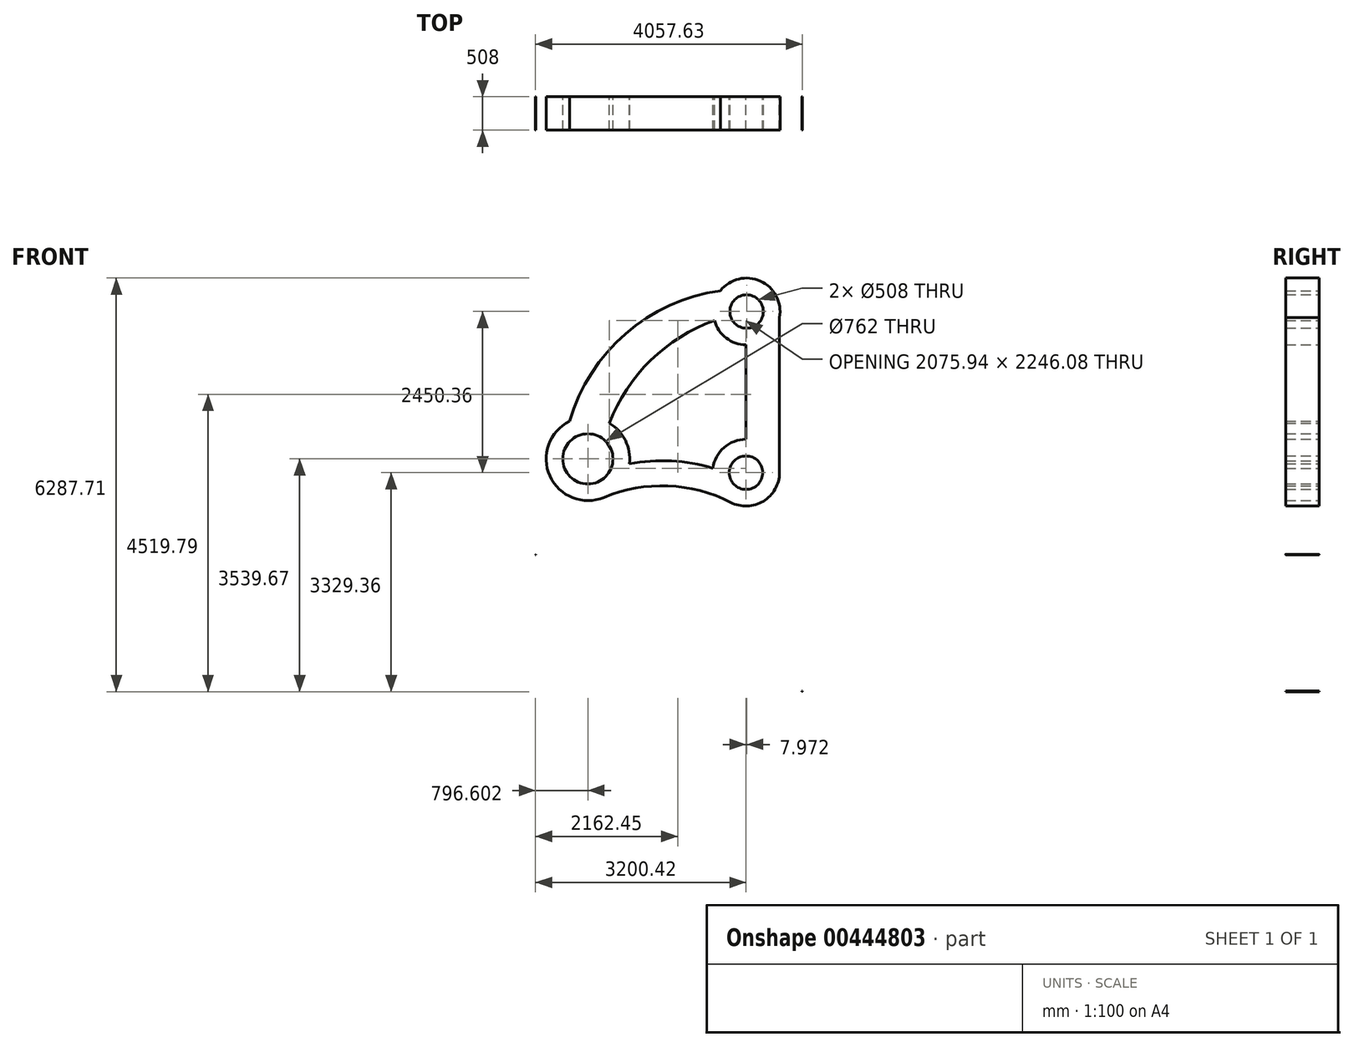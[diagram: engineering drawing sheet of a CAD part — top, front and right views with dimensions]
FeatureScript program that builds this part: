
annotation { "Feature Type Name" : "Feature", "Feature Type Description" : "" }
export const myFeature = defineFeature(function(context is Context, id is Id, definition is map)
    precondition{}
    {
        {
            var Q0;
            Q0=qCreatedBy(makeId("Front.planeOp"),FACE);
            var sketch = newSketch(context, id + "F0", { "sketchPlane" : qUnion([Q0])});
            skCircle(sketch, "E0", {"center": v(0, 0) * mm, "radius": 254 * mm});
            skArc(sketch, "E1", {"start": v(-294.4, -414) * mm, "mid": v(267.89, -431.62) * mm, "end": v(501.65, 80.07) * mm});
            skLineSegment(sketch, "E2", {"start": v(0, 0) * mm, "end": v(0, 508) * mm});
            skCircle(sketch, "E3", {"center": v(7.97, 2450.35) * mm, "radius": 254 * mm});
            skArc(sketch, "E4", {"start": v(-481.24, 2313.47) * mm, "mid": v(505.87, 2349.57) * mm, "end": v(-389.5, 2766.72) * mm});
            skLineSegment(sketch, "E5", {"start": v(508, 2540) * mm, "end": v(508, 0) * mm});
            skArc(sketch, "E6", {"start": v(-2779.82, -281.18) * mm, "mid": v(-2778.69, -292.14) * mm, "end": v(-2777.51, -303.1) * mm});
            skCircle(sketch, "E7", {"center": v(-2403.82, 210.3) * mm, "radius": 381 * mm});
            skArc(sketch, "E8", {"start": v(-1773.21, 135.7) * mm, "mid": v(-2933.68, 560.27) * mm, "end": v(-2087.68, -340.4) * mm});
            skLineSegment(sketch, "E9.0", {"start": v(501.65, 2540) * mm, "end": v(501.65, 0) * mm});
            skArc(sketch, "E10.0", {"start": v(-3196.17, -1241.99) * mm, "mid": v(-3196.17, -1242) * mm, "end": v(-3196.17, -1242) * mm});
            skArc(sketch, "E11.0", {"start": v(-3200.42, -1248.58) * mm, "mid": v(-3200.42, -1248.58) * mm, "end": v(-3200.42, -1248.58) * mm});
            skArc(sketch, "E12", {"start": v(-3196.17, -1242) * mm, "mid": v(-3198.3, -1245.28) * mm, "end": v(-3200.42, -1248.58) * mm});
            skArc(sketch, "E13.trimOffspring", {"start": v(0, 508) * mm, "mid": v(-343.2, 374.54) * mm, "end": v(-506.07, 44.28) * mm});
            skLineSegment(sketch, "E14.trimOffspring", {"start": v(-1699.09, 148.65) * mm, "end": v(-1771.23, 154.96) * mm});
            skLineSegment(sketch, "E15", {"start": v(0, 508) * mm, "end": v(0, 1942.42) * mm});
            skArc(sketch, "E16.trimOffspring", {"start": v(-3336.76, -789.98) * mm, "mid": v(-3339.3, -793.07) * mm, "end": v(-3341.82, -796.15) * mm});
            skArc(sketch, "E17.trimOffspring", {"start": v(-3196.17, -1241.99) * mm, "mid": v(-3198.3, -1245.28) * mm, "end": v(-3200.42, -1248.58) * mm});
            skArc(sketch, "E18.trimOffspring", {"start": v(846.77, -3329.36) * mm, "mid": v(848.22, -3325.71) * mm, "end": v(849.65, -3322.07) * mm});
            skArc(sketch, "E19.trimOffspring", {"start": v(846.74, -3329.36) * mm, "mid": v(848.19, -3325.72) * mm, "end": v(849.63, -3322.07) * mm});
            skArc(sketch, "E20.trimOffspring", {"start": v(854.34, -3327.42) * mm, "mid": v(855.78, -3323.77) * mm, "end": v(857.21, -3320.12) * mm});
            skArc(sketch, "E21.trimOffspring", {"start": v(-232.28, -451.79) * mm, "mid": v(-1187.2, -200.6) * mm, "end": v(-2158.97, -375.6) * mm});
            skArc(sketch, "E22.trimOffspring", {"start": v(-230.3, -452.8) * mm, "mid": v(-1186.09, -200.65) * mm, "end": v(-2158.97, -375.6) * mm});
            skArc(sketch, "E23.trimOffspring", {"start": v(-294.4, -414) * mm, "mid": v(-1262.87, -192.52) * mm, "end": v(-2234.1, -401.6) * mm});
            skArc(sketch, "E24", {"start": v(-481.24, 2313.47) * mm, "mid": v(-1449.42, 1708.5) * mm, "end": v(-2075.94, 754.1) * mm});
            skArc(sketch, "E25.trimOffspring", {"start": v(1296.97, -3181.12) * mm, "mid": v(1298, -3177.26) * mm, "end": v(1299.04, -3173.41) * mm});
            skArc(sketch, "E26.trimOffspring", {"start": v(-503.51, 67.39) * mm, "mid": v(-1134.23, 178.32) * mm, "end": v(-1773.21, 135.7) * mm});
            skArc(sketch, "E27.trimOffspring", {"start": v(-389.5, 2766.72) * mm, "mid": v(-1829.08, 2112.08) * mm, "end": v(-2682.68, 780.8) * mm});
            skArc(sketch, "E28.trimOffspring", {"start": v(846.74, -3329.36) * mm, "mid": v(850.54, -3328.4) * mm, "end": v(854.34, -3327.42) * mm});
            skArc(sketch, "E29.trimOffspring", {"start": v(849.63, -3322.07) * mm, "mid": v(853.42, -3321.1) * mm, "end": v(857.21, -3320.12) * mm});
            skSolve(sketch);
        }
        {
            var Q0;
            Q0 = qSketchRegion(id + "F0", true);
            extrude(context, id + "F1", {"entities" : qUnion([Q0]), "depth" : 508 * mm});
        }
    });
